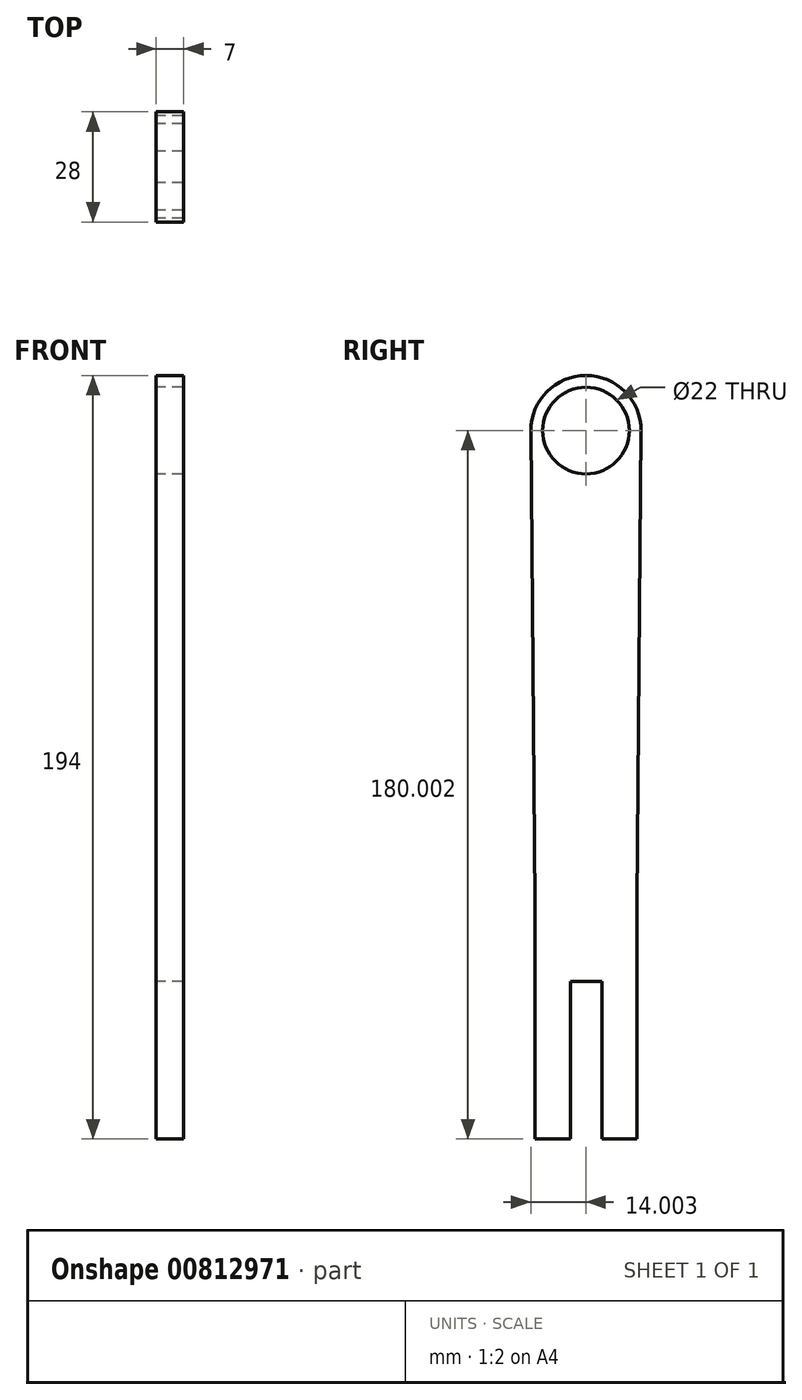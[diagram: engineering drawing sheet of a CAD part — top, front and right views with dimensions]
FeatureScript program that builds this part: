
annotation { "Feature Type Name" : "Feature", "Feature Type Description" : "" }
export const myFeature = defineFeature(function(context is Context, id is Id, definition is map)
    precondition{}
    {
        {
            var Q0;
            Q0=qCreatedBy(makeId("Right.planeOp"),FACE);
            var sketch = newSketch(context, id + "F0", { "sketchPlane" : qUnion([Q0])});
            skLineSegment(sketch, "E0", {"start": v(-57.83, 20.2) * mm, "end": v(-49.83, 20.2) * mm});
            skLineSegment(sketch, "E1", {"start": v(-49.83, 20.2) * mm, "end": v(-49.83, -19.8) * mm});
            skLineSegment(sketch, "E2", {"start": v(-49.83, -19.8) * mm, "end": v(-40.83, -19.8) * mm});
            skLineSegment(sketch, "E3", {"start": v(-40.83, -19.8) * mm, "end": v(-40.83, 40.2) * mm});
            skLineSegment(sketch, "E4", {"start": v(-57.83, 20.2) * mm, "end": v(-57.83, -19.8) * mm});
            skLineSegment(sketch, "E5", {"start": v(-57.83, -19.8) * mm, "end": v(-66.83, -19.8) * mm});
            skLineSegment(sketch, "E6", {"start": v(-66.83, -19.8) * mm, "end": v(-66.83, 40.2) * mm});
            skLineSegment(sketch, "E7", {"start": v(-53.83, 149.2) * mm, "end": v(-53.83, 160.2) * mm});
            skCircle(sketch, "E8", {"center": v(-53.83, 160.2) * mm, "radius": 11 * mm});
            skArc(sketch, "E9", {"start": v(-39.83, 159.96) * mm, "mid": v(-53.83, 174.2) * mm, "end": v(-67.82, 159.96) * mm});
            skLineSegment(sketch, "E10", {"start": v(-53.83, 160.2) * mm, "end": v(-64.83, 160.2) * mm});
            skLineSegment(sketch, "E11", {"start": v(-53.83, 160.2) * mm, "end": v(-42.83, 160.2) * mm});
            skLineSegment(sketch, "E12", {"start": v(-67.83, 160.2) * mm, "end": v(-66.83, 40.2) * mm});
            skLineSegment(sketch, "E13", {"start": v(-40.83, 40.2) * mm, "end": v(-39.83, 160.2) * mm});
            skPoint(sketch, "E14.orphan", {"position": v(-53.83, 40.2) * mm});
            skSolve(sketch);
        }
        {
            var Q0;
            Q0=makeQuery(id+"F0.imprint","IMPRINT",FACE,{"disambiguationData":[TD([[makeQuery(id+"F0.imprint","IMPRINT",EDGE,{"derivedFrom":sQuery(id+"F0.wireOp",EDGE,"E0")}),1.0]])]});
            extrude(context, id + "F1", {"entities" : qUnion([Q0]), "depth" : 7 * mm, "offsetDistance" : 25 * mm});
        }
    });
